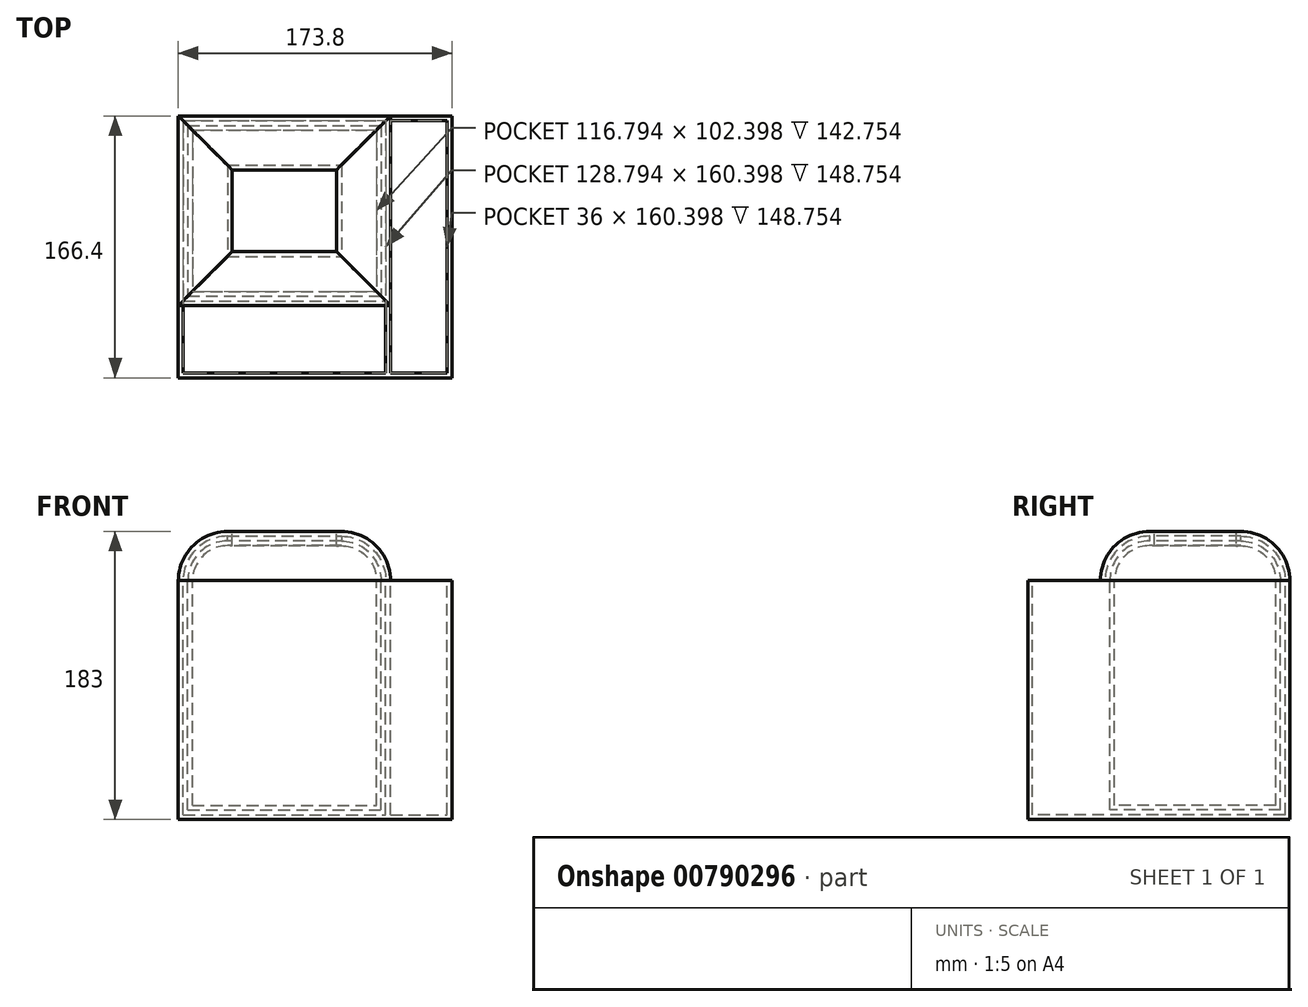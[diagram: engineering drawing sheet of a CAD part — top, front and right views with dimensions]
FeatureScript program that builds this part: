
annotation { "Feature Type Name" : "Feature", "Feature Type Description" : "" }
export const myFeature = defineFeature(function(context is Context, id is Id, definition is map)
    precondition{}
    {
        {
            var Q0;
            Q0=qCreatedBy(makeId("Top.planeOp"),FACE);
            var sketch = newSketch(context, id + "F0", { "sketchPlane" : qUnion([Q0])});
            skLineSegment(sketch, "E0.bottom", {"start": v(-9.7, 57.2) * mm, "end": v(9.7, 57.2) * mm});
            skLineSegment(sketch, "E0.top", {"start": v(-9.7, -57.2) * mm, "end": v(9.7, -57.2) * mm});
            skLineSegment(sketch, "E0.left", {"start": v(-9.7, 57.2) * mm, "end": v(-9.7, -57.2) * mm});
            skLineSegment(sketch, "E0.right", {"start": v(9.7, 57.2) * mm, "end": v(9.7, -57.2) * mm});
            skPoint(sketch, "E0.middle", {"position": v(0, 0) * mm});
            skSolve(sketch);
        }
        {
            var Q0;
            Q0=makeQuery(id+"F0.imprint","IMPRINT",FACE,{"disambiguationData":[TD([[makeQuery(id+"F0.imprint","IMPRINT",EDGE,{"derivedFrom":sQuery(id+"F0.wireOp",EDGE,"E0.bottom")}),-1.0]])]});
            extrude(context, id + "F1", {"entities" : qUnion([Q0]), "oppositeDirection" : true, "depth" : (80) * mm, "offsetDistance" : 25 * mm});
        }
        {
            var Q0;
            Q0=makeQuery(id+"F1.opExtrude","SWEPT_FACE",FACE,{"disambiguationData":[OSD([sQuery(id+"F0.wireOp",EDGE,"E0.left")])]});
            extrude(context, id + "F2", {"entities" : qUnion([Q0]), "operationType" : NewBodyOperationType.ADD, "depth" : 60.4 * mm, "offsetDistance" : 25 * mm});
        }
        {
            var Q0;
            Q0=makeQuery(id+"F1.opExtrude","SWEPT_FACE",FACE,{"disambiguationData":[OSD([sQuery(id+"F0.wireOp",EDGE,"E0.right")])]});
            extrude(context, id + "F3", {"entities" : qUnion([Q0]), "operationType" : NewBodyOperationType.ADD, "depth" : 49 * mm, "offsetDistance" : 25 * mm});
        }
        {
            var Q0;
            {var subQ0=sQuery(id+"F0.wireOp",EDGE,"E0.right");var subQ1=sQuery(id+"F0.wireOp",EDGE,"E0.left");Q0=makeQuery(id+"F3.boolean.opBoolean","MERGE",FACE,{"derivedFrom":[makeQuery(id+"F2.boolean.opBoolean","MERGE",FACE,{"derivedFrom":[makeQuery(id+"F1.opExtrude","CAP_FACE",FACE,{"disambiguationData":[OSD([sQuery(id+"F0.wireOp",EDGE,"E0.bottom"),sQuery(id+"F0.wireOp",EDGE,"E0.top"),subQ1,subQ0])],"isStart":true}),makeQuery(id+"F2.opExtrude","SWEPT_FACE",FACE,{"disambiguationData":[OSD([subQ1]),TDD([makeQuery(id+"F1.opExtrude","CAP_EDGE",EDGE,{"disambiguationData":[OSD([subQ1])],"isStart":true})])]})]}),makeQuery(id+"F3.opExtrude","SWEPT_FACE",FACE,{"disambiguationData":[OSD([subQ0]),TDD([makeQuery(id+"F1.opExtrude","CAP_EDGE",EDGE,{"disambiguationData":[OSD([subQ0])],"isStart":true})])]})]});}
            extrude(context, id + "F4", {"entities" : qUnion([Q0]), "operationType" : NewBodyOperationType.ADD, "depth" : 97 * mm, "offsetDistance" : 25 * mm});
        }
        {
            var Q0;
            Q0=makeQuery(id+"F4.opExtrude","CAP_FACE",FACE,{"disambiguationData":[OSD([sQuery(id+"F0.wireOp",EDGE,"E0.bottom"),sQuery(id+"F0.wireOp",EDGE,"E0.top"),sQuery(id+"F0.wireOp",EDGE,"E0.left"),sQuery(id+"F0.wireOp",EDGE,"E0.right")])],"isStart":false});
            fillet(context, id + "F5", {"entities" : qUnion([Q0]), "radius" : 28.25 * mm, "tangentPropagation" : true, "allowEdgeOverflow" : false});
        }
        {
            var Q0;
            Q0=makeQuery(id+"F4.opExtrude","CAP_FACE",FACE,{"disambiguationData":[OSD([sQuery(id+"F0.wireOp",EDGE,"E0.bottom"),sQuery(id+"F0.wireOp",EDGE,"E0.top"),sQuery(id+"F0.wireOp",EDGE,"E0.left"),sQuery(id+"F0.wireOp",EDGE,"E0.right")])],"isStart":false});
            shell(context, id + "F6", {"entities" : qUnion([Q0]), "thickness" : 3 * mm});
        }
        {
            var Q0;
            {var subQ0=sQuery(id+"F0.wireOp",EDGE,"E0.right");var subQ1=sQuery(id+"F0.wireOp",EDGE,"E0.left");var subQ2=sQuery(id+"F0.wireOp",EDGE,"E0.top");Q0=makeQuery(id+"F4.boolean.opBoolean","MERGE",FACE,{"derivedFrom":[makeQuery(id+"F3.boolean.opBoolean","MERGE",FACE,{"derivedFrom":[makeQuery(id+"F2.boolean.opBoolean","MERGE",FACE,{"derivedFrom":[makeQuery(id+"F1.opExtrude","SWEPT_FACE",FACE,{"disambiguationData":[OSD([subQ2])]}),makeQuery(id+"F2.opExtrude","SWEPT_FACE",FACE,{"disambiguationData":[OSD([subQ2,subQ1])]})]}),makeQuery(id+"F3.opExtrude","SWEPT_FACE",FACE,{"disambiguationData":[OSD([subQ2,subQ0])]})]}),makeQuery(id+"F4.opExtrude","SWEPT_FACE",FACE,{"disambiguationData":[OSD([subQ2,subQ1,subQ0])]})]});}
            extrude(context, id + "F7", {"entities" : qUnion([Q0]), "operationType" : NewBodyOperationType.ADD, "depth" : 46 * mm, "offsetDistance" : 25 * mm});
        }
        {
            var Q0;
            {var subQ0=sQuery(id+"F0.wireOp",EDGE,"E0.right");var subQ1=sQuery(id+"F0.wireOp",EDGE,"E0.left");var subQ2=sQuery(id+"F0.wireOp",EDGE,"E0.top");Q0=makeQuery(id+"F7.opExtrude","SWEPT_FACE",FACE,{"disambiguationData":[OSD([subQ2,subQ1,subQ0]),TDD([makeQuery(id+"F5.opFillet","BLEND_EDGE",EDGE,{"blendedFrom":[makeQuery(id+"F4.opExtrude","CAP_EDGE",EDGE,{"disambiguationData":[OSD([subQ2,subQ1,subQ0])],"isStart":false}),makeQuery(id+"F4.boolean.opBoolean","MERGE",FACE,{"derivedFrom":[makeQuery(id+"F3.boolean.opBoolean","MERGE",FACE,{"derivedFrom":[makeQuery(id+"F2.boolean.opBoolean","MERGE",FACE,{"derivedFrom":[makeQuery(id+"F1.opExtrude","SWEPT_FACE",FACE,{"disambiguationData":[OSD([subQ2])]}),makeQuery(id+"F2.opExtrude","SWEPT_FACE",FACE,{"disambiguationData":[OSD([subQ2,subQ1])]})]}),makeQuery(id+"F3.opExtrude","SWEPT_FACE",FACE,{"disambiguationData":[OSD([subQ2,subQ0])]})]}),makeQuery(id+"F4.opExtrude","SWEPT_FACE",FACE,{"disambiguationData":[OSD([subQ2,subQ1,subQ0])]})]})],"blendedInto":[makeQuery(id+"F4.boolean.opBoolean","MERGE",FACE,{"derivedFrom":[makeQuery(id+"F3.boolean.opBoolean","MERGE",FACE,{"derivedFrom":[makeQuery(id+"F2.boolean.opBoolean","MERGE",FACE,{"derivedFrom":[makeQuery(id+"F1.opExtrude","SWEPT_FACE",FACE,{"disambiguationData":[OSD([subQ2])]}),makeQuery(id+"F2.opExtrude","SWEPT_FACE",FACE,{"disambiguationData":[OSD([subQ2,subQ1])]})]}),makeQuery(id+"F3.opExtrude","SWEPT_FACE",FACE,{"disambiguationData":[OSD([subQ2,subQ0])]})]}),makeQuery(id+"F4.opExtrude","SWEPT_FACE",FACE,{"disambiguationData":[OSD([subQ2,subQ1,subQ0])]})]})]})])]});}
            shell(context, id + "F8", {"entities" : qUnion([Q0]), "thickness" : 3 * mm, "oppositeDirection" : true});
        }
        {
            var Q0;
            {var subQ0=sQuery(id+"F0.wireOp",EDGE,"E0.right");Q0=makeQuery(id+"F7.boolean.opBoolean","MERGE",FACE,{"derivedFrom":[makeQuery(id+"F4.boolean.opBoolean","MERGE",FACE,{"derivedFrom":[makeQuery(id+"F3.opExtrude","CAP_FACE",FACE,{"disambiguationData":[OSD([subQ0])],"isStart":false}),makeQuery(id+"F4.opExtrude","SWEPT_FACE",FACE,{"disambiguationData":[OSD([subQ0])]})]}),makeQuery(id+"F7.opExtrude","SWEPT_FACE",FACE,{"disambiguationData":[OSD([sQuery(id+"F0.wireOp",EDGE,"E0.top"),subQ0])]})]});}
            extrude(context, id + "F9", {"entities" : qUnion([Q0]), "operationType" : NewBodyOperationType.ADD, "depth" : 39 * mm, "offsetDistance" : 25 * mm});
        }
        {
            var Q0;
            {var subQ0=sQuery(id+"F0.wireOp",EDGE,"E0.right");var subQ1=sQuery(id+"F0.wireOp",EDGE,"E0.left");var subQ2=sQuery(id+"F0.wireOp",EDGE,"E0.top");Q0=makeQuery(id+"F9.boolean.opBoolean","MERGE",FACE,{"derivedFrom":[makeQuery(id+"F7.opExtrude","SWEPT_FACE",FACE,{"disambiguationData":[OSD([subQ2,subQ1,subQ0]),TDD([makeQuery(id+"F5.opFillet","BLEND_EDGE",EDGE,{"blendedFrom":[makeQuery(id+"F4.opExtrude","CAP_EDGE",EDGE,{"disambiguationData":[OSD([subQ2,subQ1,subQ0])],"isStart":false}),makeQuery(id+"F4.boolean.opBoolean","MERGE",FACE,{"derivedFrom":[makeQuery(id+"F3.boolean.opBoolean","MERGE",FACE,{"derivedFrom":[makeQuery(id+"F2.boolean.opBoolean","MERGE",FACE,{"derivedFrom":[makeQuery(id+"F1.opExtrude","SWEPT_FACE",FACE,{"disambiguationData":[OSD([subQ2])]}),makeQuery(id+"F2.opExtrude","SWEPT_FACE",FACE,{"disambiguationData":[OSD([subQ2,subQ1])]})]}),makeQuery(id+"F3.opExtrude","SWEPT_FACE",FACE,{"disambiguationData":[OSD([subQ2,subQ0])]})]}),makeQuery(id+"F4.opExtrude","SWEPT_FACE",FACE,{"disambiguationData":[OSD([subQ2,subQ1,subQ0])]})]})],"blendedInto":[makeQuery(id+"F4.boolean.opBoolean","MERGE",FACE,{"derivedFrom":[makeQuery(id+"F3.boolean.opBoolean","MERGE",FACE,{"derivedFrom":[makeQuery(id+"F2.boolean.opBoolean","MERGE",FACE,{"derivedFrom":[makeQuery(id+"F1.opExtrude","SWEPT_FACE",FACE,{"disambiguationData":[OSD([subQ2])]}),makeQuery(id+"F2.opExtrude","SWEPT_FACE",FACE,{"disambiguationData":[OSD([subQ2,subQ1])]})]}),makeQuery(id+"F3.opExtrude","SWEPT_FACE",FACE,{"disambiguationData":[OSD([subQ2,subQ0])]})]}),makeQuery(id+"F4.opExtrude","SWEPT_FACE",FACE,{"disambiguationData":[OSD([subQ2,subQ1,subQ0])]})]})]})])]}),makeQuery(id+"F9.opExtrude","SWEPT_FACE",FACE,{"disambiguationData":[OSD([subQ2,subQ1,subQ0])]})]});}
            shell(context, id + "F10", {"entities" : qUnion([Q0]), "thickness" : 3 * mm});
        }
    });
